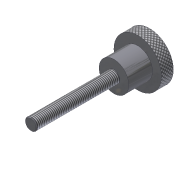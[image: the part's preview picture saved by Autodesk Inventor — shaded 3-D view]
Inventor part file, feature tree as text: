
AUTODESK INVENTOR PART (.ipt)
format: ipt  version: 2012 (Build 160160000, 160)  size: 92,160 bytes
history: native  units: in
note: dims shown in document units (in); Inventor stores cm internally (conversion verified against a paired STEP export)
features: extrude x3, sketch x3, thread x1, chamfer x1
ambient origin geometry x8: Origin, YZ Plane, XZ Plane, XY Plane, X Axis, Y Axis, Z Axis, Center Point
bodies: Solid1 (feature_tree)
feature tree (8):
  extrude  "Extrusion1"  Depth=0.25in TaperAngle=0.0deg
  extrude  "Extrusion2"  Depth=0.5in TaperAngle=0.0deg
  extrude  "Extrusion3"  Depth=1.75in TaperAngle=0.0deg
  thread  "Thread1"  [1 undecoded]
  chamfer  "Chamfer1"  [1 undecoded]
  sketch  "Sketch1"  dims[d0=1.0in d1=0.25in d2=0.0in]
  sketch  "Sketch2"  dims[d3=0.625in d4=0.5in d5=0.0in]
  sketch  "Sketch3"  dims[d6=0.25in d7=1.75in d8=0.0in d9=1.0in d10=0.0in d11=0.015in d12=0.125in d13=45.0deg]
note: 2 required parameter values undecoded (feature->parameter linkage not recoverable at this tier; creation-order binding heuristic only, values carry confidence <= 0.55)
